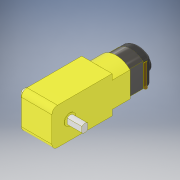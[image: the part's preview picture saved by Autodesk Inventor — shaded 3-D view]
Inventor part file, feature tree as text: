
AUTODESK INVENTOR PART (.ipt)
format: ipt  version: 2020 (Build 240018000, 18) ContinuousBuild 0  size: 288,256 bytes
history: native  units: in
note: dims shown in document units (in); Inventor stores cm internally (conversion verified against a paired STEP export)
features: extrude x11, sketch x11, projected_geometry x5, fillet x3, mirror x1
ambient origin geometry x8: Origin, YZ Plane, XZ Plane, XY Plane, X Axis, Y Axis, Z Axis, Center Point
bodies: Solid1 (feature_tree), Solid2 (feature_tree), Solid3 (feature_tree), Solid4 (feature_tree)
feature tree (31):
  extrude  "Extrusion1"  Depth=0.8858in
  fillet  "Fillet1"  Radius=1.4567in
  extrude  "Extrusion2"  Depth=0.1378in
  extrude  "Extrusion3"  Depth=0.6693in
  extrude  "Extrusion4"  Depth=0.0394in
  extrude  "Extrusion5"  Depth=0.1969in TaperAngle=0.0deg
  extrude  "Extrusion6"  Depth=0.4331in
  extrude  "Extrusion7"  Depth=0.1969in
  mirror  "Mirror1"
  extrude  "Extrusion8"  Depth=0.1457in
  fillet  "Fillet2"  Radius=0.0728in
  extrude  "Extrusion9"  Depth=0.3543in
  extrude  "Extrusion10"  Depth=0.0591in TaperAngle=0.0deg
  extrude  "Extrusion11"  Depth=0.3937in
  fillet  "Fillet3"  Radius=0.1673in
  sketch  "Sketch1"  dims[d0=0.7362in d1=0.8858in d2=1.4567in d3=0.0in]
  sketch  "Sketch2"  dims[d4=0.1339in d5=0.1378in]
  sketch  "Sketch3"  dims[d6=0.1378in d7=0.6693in]
  projected_geometry  "Projected Loop1"
  sketch  "Sketch4"  dims[d8=0.4331in d9=0.0in d10=0.0394in]
  projected_geometry  "Projected Loop2"
  sketch  "Sketch5"  dims[d11=0.3543in d12=0.0in d13=0.1969in d14=0.0in]
  sketch  "Sketch6"  dims[d15=0.4331in d16=0.2756in]
  projected_geometry  "Projected Loop3"
  sketch  "Sketch7"  dims[d17=0.0098in d18=0.0in d19=0.1969in]
  projected_geometry  "Projected Loop4"
  sketch  "Sketch8"  dims[d20=0.3543in d21=0.0in d22=0.1457in d23=0.0728in]
  sketch  "Sketch9"  dims[d25=0.3543in d26=0.0in d27=0.1575in]
  projected_geometry  "Projected Loop5"
  sketch  "Sketch10"  dims[d28=0.8661in d29=0.0591in d30=0.0in]
  sketch  "Sketch11"  dims[d31=0.0787in d32=0.3937in d33=0.1673in d34=0.0984in d35=0.0in d36=0.0787in d37=0.0394in d38=0.0in d39=0.0098in d40=0.5906in d41=0.0098in d42=0.0394in d43=0.0787in d44=0.0in d45=0.0394in]
